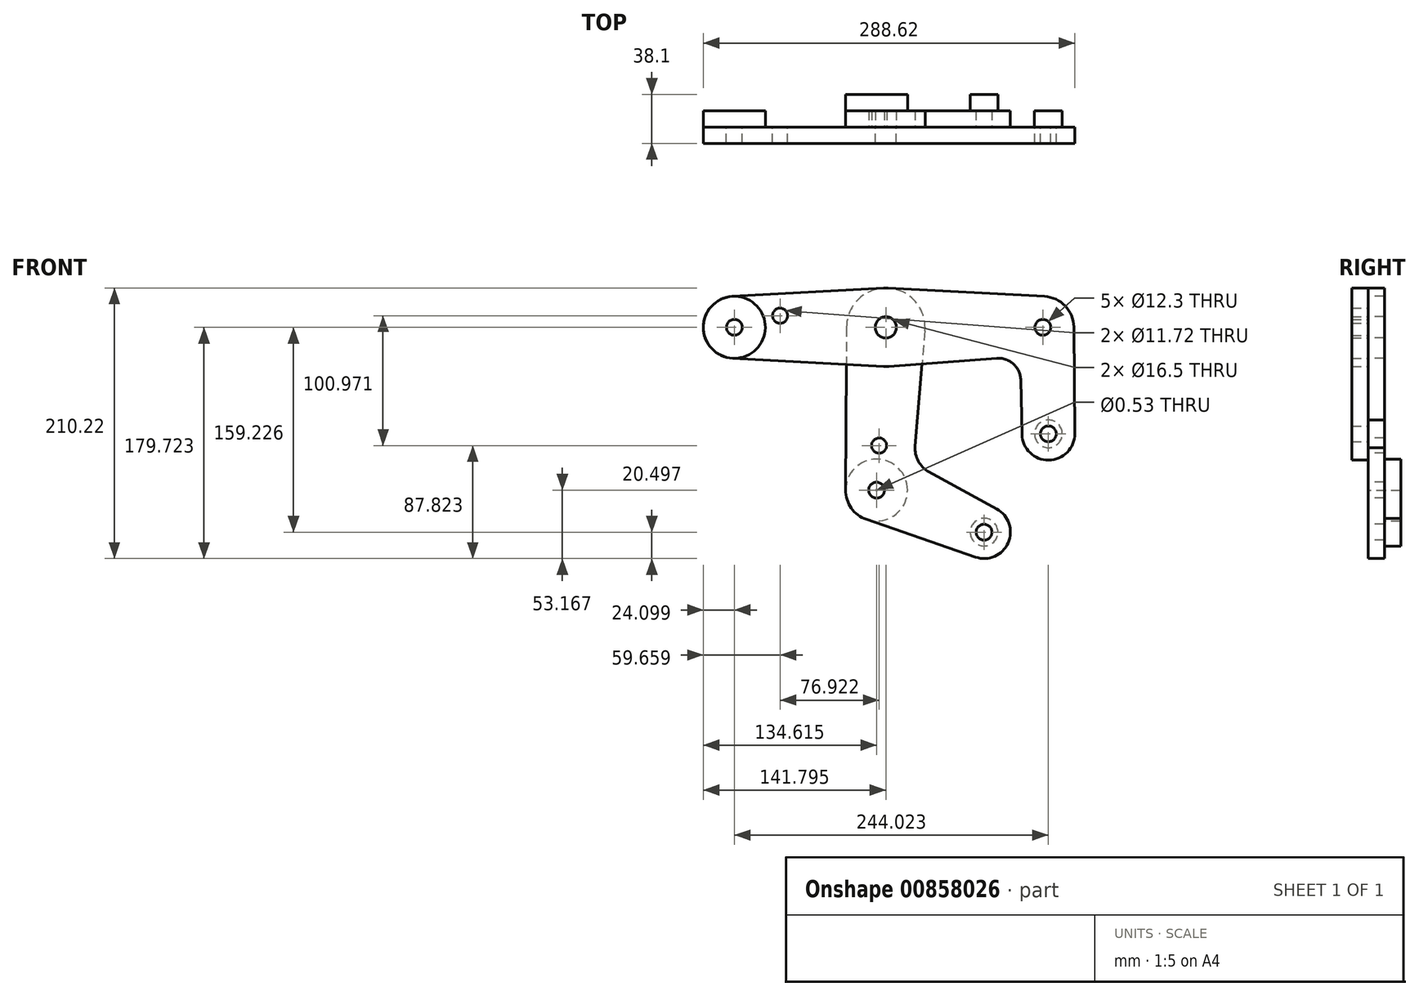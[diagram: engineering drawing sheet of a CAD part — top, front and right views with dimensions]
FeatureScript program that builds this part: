
annotation { "Feature Type Name" : "Feature", "Feature Type Description" : "" }
export const myFeature = defineFeature(function(context is Context, id is Id, definition is map)
    precondition{}
    {
        {
            var Q0;
            Q0=qCreatedBy(makeId("Front.planeOp"),FACE);
            var sketch = newSketch(context, id + "F0", { "sketchPlane" : qUnion([Q0])});
            skCircle(sketch, "E0", {"center": v(-43.4, 53.77) * mm, "radius": 30.5 * mm});
            skCircle(sketch, "E1", {"center": v(-161.1, 53.77) * mm, "radius": 24.1 * mm});
            skCircle(sketch, "E2", {"center": v(78.57, 53.77) * mm, "radius": 24.1 * mm});
            skCircle(sketch, "E3", {"center": v(-50.59, -72.78) * mm, "radius": 24.1 * mm});
            skCircle(sketch, "E4", {"center": v(32.9, -105.45) * mm, "radius": 20.5 * mm});
            skCircle(sketch, "E5", {"center": v(82.92, -29) * mm, "radius": 20.5 * mm});
            skCircle(sketch, "E6", {"center": v(-125.54, 62.84) * mm, "radius": 5.86 * mm});
            skCircle(sketch, "E7", {"center": v(-48.62, -38.13) * mm, "radius": 5.86 * mm});
            skLineSegment(sketch, "E8", {"start": v(-161.1, 53.77) * mm, "end": v(78.57, 53.77) * mm, "construction": true});
            skLineSegment(sketch, "E9", {"start": v(82.92, -29) * mm, "end": v(78.57, 53.77) * mm, "construction": true});
            skLineSegment(sketch, "E10", {"start": v(-50.59, -72.78) * mm, "end": v(32.9, -105.45) * mm, "construction": true});
            skLineSegment(sketch, "E11", {"start": v(-58.46, -95.56) * mm, "end": v(26.2, -124.83) * mm});
            skLineSegment(sketch, "E12", {"start": v(-162.41, 77.83) * mm, "end": v(-45.06, 84.22) * mm});
            skLineSegment(sketch, "E13", {"start": v(-41.8, 84.22) * mm, "end": v(79.84, 77.84) * mm});
            skLineSegment(sketch, "E14", {"start": v(-162.41, 29.71) * mm, "end": v(-45.06, 23.32) * mm});
            skLineSegment(sketch, "E15", {"start": v(-43.4, 53.77) * mm, "end": v(-50.59, -72.78) * mm, "construction": true});
            skLineSegment(sketch, "E16", {"start": v(-73.9, 53.96) * mm, "end": v(-74.68, -72.63) * mm});
            skLineSegment(sketch, "E17", {"start": v(102.67, 54) * mm, "end": v(103.42, -28.82) * mm});
            skCircle(sketch, "E18", {"center": v(-161.1, 53.77) * mm, "radius": 6.15 * mm});
            skCircle(sketch, "E19", {"center": v(-43.4, 53.77) * mm, "radius": 6.15 * mm});
            skCircle(sketch, "E20", {"center": v(78.57, 53.77) * mm, "radius": 6.15 * mm});
            skCircle(sketch, "E21", {"center": v(82.92, -29) * mm, "radius": 6.15 * mm});
            skCircle(sketch, "E22", {"center": v(32.9, -105.45) * mm, "radius": 6.15 * mm});
            skCircle(sketch, "E23", {"center": v(-50.59, -72.78) * mm, "radius": 6.15 * mm});
            skCircle(sketch, "E24", {"center": v(-43.4, 53.77) * mm, "radius": 8.25 * mm});
            skLineSegment(sketch, "E25", {"start": v(-41.08, 23.37) * mm, "end": v(42.63, 29.77) * mm});
            skLineSegment(sketch, "E26", {"start": v(62.43, -29.48) * mm, "end": v(61.45, 12.74) * mm});
            skArc(sketch, "E27", {"start": v(42.63, 29.77) * mm, "mid": v(55.7, 25.3) * mm, "end": v(61.45, 12.74) * mm});
            skLineSegment(sketch, "E28", {"start": v(-13.02, 51.2) * mm, "end": v(-20.63, -38.68) * mm});
            skLineSegment(sketch, "E29", {"start": v(42.76, -87.48) * mm, "end": v(-9.95, -58.58) * mm});
            skArc(sketch, "E30", {"start": v(-20.63, -38.68) * mm, "mid": v(-18.24, -50.22) * mm, "end": v(-9.95, -58.58) * mm});
            skSolve(sketch);
        }
        {
            var Q0;
            Q0=makeQuery(id+"F0.imprint","IMPRINT",FACE,{"disambiguationData":[TD([[makeQuery(id+"F0.imprint","IMPRINT",EDGE,{"derivedFrom":sQuery(id+"F0.wireOp",EDGE,"E18")}),-1.0]])]});
            var Q1;
            Q1=makeQuery(id+"F0.imprint","IMPRINT",FACE,{"disambiguationData":[TD([[makeQuery(id+"F0.imprint","IMPRINT",EDGE,{"derivedFrom":sQuery(id+"F0.wireOp",EDGE,"E6")}),-1.0]])]});
            var Q2;
            {var subQ0=sQuery(id+"F0.wireOp",EDGE,"E14");var subQ1=sQuery(id+"F0.wireOp",EDGE,"E0");var subQ2=makeQuery(id+"F0.imprint","INTERSECT",VERTEX,{"derivedFrom":[subQ1,subQ0]});Q2=makeQuery(id+"F0.imprint","IMPRINT",FACE,{"disambiguationData":[TD([[makeQuery(id+"F0.imprint","IMPRINT",EDGE,{"disambiguationData":[TD([[subQ2,1.0]])],"derivedFrom":subQ1}),-1.0]])]});}
            var Q3;
            Q3=makeQuery(id+"F0.imprint","IMPRINT",FACE,{"disambiguationData":[TD([[makeQuery(id+"F0.imprint","IMPRINT",EDGE,{"derivedFrom":sQuery(id+"F0.wireOp",EDGE,"E24")}),-1.0]])]});
            var Q4;
            {var subQ0=sQuery(id+"F0.wireOp",EDGE,"E25");var subQ1=sQuery(id+"F0.wireOp",EDGE,"E0");var subQ2=makeQuery(id+"F0.imprint","INTERSECT",VERTEX,{"derivedFrom":[subQ1,subQ0]});Q4=makeQuery(id+"F0.imprint","IMPRINT",FACE,{"disambiguationData":[TD([[makeQuery(id+"F0.imprint","IMPRINT",EDGE,{"disambiguationData":[TD([[subQ2,-1.0]])],"derivedFrom":subQ1}),-1.0]])]});}
            var Q5;
            {var subQ4=sQuery(id+"F0.wireOp",EDGE,"E13");Q5=makeQuery(id+"F0.imprint","IMPRINT",FACE,{"disambiguationData":[TD([[makeQuery(id+"F0.imprint","IMPRINT",EDGE,{"derivedFrom":subQ4}),-1.0]])]});}
            var Q6;
            Q6=makeQuery(id+"F0.imprint","IMPRINT",FACE,{"disambiguationData":[TD([[makeQuery(id+"F0.imprint","IMPRINT",EDGE,{"derivedFrom":sQuery(id+"F0.wireOp",EDGE,"E20")}),-1.0]])]});
            var Q7;
            Q7=makeQuery(id+"F0.imprint","IMPRINT",FACE,{"disambiguationData":[TD([[makeQuery(id+"F0.imprint","IMPRINT",EDGE,{"derivedFrom":sQuery(id+"F0.wireOp",EDGE,"E21")}),-1.0]])]});
            extrude(context, id + "F1", {"entities" : qUnion([Q0, Q1, Q2, Q3, Q4, Q5, Q6, Q7]), "depth" : 12.7 * mm, "offsetDistance" : 25 * mm});
        }
        {
            var Q0;
            Q0=makeQuery(id+"F0.imprint","IMPRINT",FACE,{"disambiguationData":[TD([[makeQuery(id+"F0.imprint","IMPRINT",EDGE,{"derivedFrom":sQuery(id+"F0.wireOp",EDGE,"E24")}),-1.0]])]});
            var Q1;
            {var subQ0=sQuery(id+"F0.wireOp",EDGE,"E25");var subQ1=sQuery(id+"F0.wireOp",EDGE,"E0");var subQ2=makeQuery(id+"F0.imprint","INTERSECT",VERTEX,{"derivedFrom":[subQ1,subQ0]});Q1=makeQuery(id+"F0.imprint","IMPRINT",FACE,{"disambiguationData":[TD([[makeQuery(id+"F0.imprint","IMPRINT",EDGE,{"disambiguationData":[TD([[subQ2,-1.0]])],"derivedFrom":subQ1}),-1.0]])]});}
            var Q2;
            {var subQ0=sQuery(id+"F0.wireOp",EDGE,"E14");var subQ1=sQuery(id+"F0.wireOp",EDGE,"E0");var subQ2=makeQuery(id+"F0.imprint","INTERSECT",VERTEX,{"derivedFrom":[subQ1,subQ0]});Q2=makeQuery(id+"F0.imprint","IMPRINT",FACE,{"disambiguationData":[TD([[makeQuery(id+"F0.imprint","IMPRINT",EDGE,{"disambiguationData":[TD([[subQ2,1.0]])],"derivedFrom":subQ1}),-1.0]])]});}
            var Q3;
            Q3=makeQuery(id+"F0.imprint","IMPRINT",FACE,{"disambiguationData":[TD([[makeQuery(id+"F0.imprint","IMPRINT",EDGE,{"derivedFrom":sQuery(id+"F0.wireOp",EDGE,"E7")}),-1.0]])]});
            var Q4;
            Q4=makeQuery(id+"F0.imprint","IMPRINT",FACE,{"disambiguationData":[TD([[makeQuery(id+"F0.imprint","IMPRINT",EDGE,{"derivedFrom":sQuery(id+"F0.wireOp",EDGE,"E23")}),-1.0]])]});
            var Q5;
            Q5=makeQuery(id+"F0.imprint","IMPRINT",FACE,{"disambiguationData":[TD([[makeQuery(id+"F0.imprint","IMPRINT",EDGE,{"derivedFrom":sQuery(id+"F0.wireOp",EDGE,"E22")}),-1.0]])]});
            extrude(context, id + "F2", {"entities" : qUnion([Q0, Q1, Q2, Q3, Q4, Q5]), "oppositeDirection" : true, "depth" : 12.7 * mm, "offsetDistance" : 25 * mm});
        }
        {
            var Q0;
            Q0=makeQuery(id+"F1.opExtrude","CAP_FACE",FACE,{"disambiguationData":[OSD([sQuery(id+"F0.wireOp",EDGE,"E0"),sQuery(id+"F0.wireOp",EDGE,"E1"),sQuery(id+"F0.wireOp",EDGE,"E2"),sQuery(id+"F0.wireOp",EDGE,"E5"),sQuery(id+"F0.wireOp",EDGE,"E6"),sQuery(id+"F0.wireOp",EDGE,"E12"),sQuery(id+"F0.wireOp",EDGE,"E13"),sQuery(id+"F0.wireOp",EDGE,"E14"),sQuery(id+"F0.wireOp",EDGE,"E17"),sQuery(id+"F0.wireOp",EDGE,"E18"),sQuery(id+"F0.wireOp",EDGE,"E20"),sQuery(id+"F0.wireOp",EDGE,"E21"),sQuery(id+"F0.wireOp",EDGE,"E24"),sQuery(id+"F0.wireOp",EDGE,"E25"),sQuery(id+"F0.wireOp",EDGE,"E26"),sQuery(id+"F0.wireOp",EDGE,"E27")])],"isStart":false});
            var sketch = newSketch(context, id + "F3", { "sketchPlane" : qUnion([Q0])});
            skCircle(sketch, "E31", {"center": v(82.92, -29) * mm, "radius": 10.76 * mm});
            skCircle(sketch, "E32", {"center": v(-161.1, 53.77) * mm, "radius": 24.1 * mm});
            skSolve(sketch);
        }
        {
            var Q0;
            Q0=makeQuery(id+"F0.imprint","IMPRINT",FACE,{"disambiguationData":[TD([[makeQuery(id+"F0.imprint","IMPRINT",EDGE,{"derivedFrom":sQuery(id+"F0.wireOp",EDGE,"E7")}),-1.0]])]});
            var sketch = newSketch(context, id + "F4", { "sketchPlane" : qUnion([Q0])});
            skCircle(sketch, "E33", {"center": v(-50.59, -72.78) * mm, "radius": 24.06 * mm});
            skCircle(sketch, "E34", {"center": v(-50.59, -72.78) * mm, "radius": 0.27 * mm});
            skCircle(sketch, "E35", {"center": v(32.9, -105.45) * mm, "radius": 10.76 * mm});
            skSolve(sketch);
        }
        {
            var Q0;
            Q0 = qSketchRegion(id + "F3", true);
            var Q1;
            Q1 = qSketchRegion(id + "F4", true);
            extrude(context, id + "F5", {"entities" : qUnion([Q0, Q1]), "oppositeDirection" : true, "depth" : 25.4 * mm, "offsetDistance" : 25 * mm});
        }
        {
            var Q0;
            Q0=makeQuery(id+"F1.opExtrude","SWEPT_BODY",BODY,{"disambiguationData":[OSD([sQuery(id+"F0.wireOp",EDGE,"E0"),sQuery(id+"F0.wireOp",EDGE,"E1"),sQuery(id+"F0.wireOp",EDGE,"E2"),sQuery(id+"F0.wireOp",EDGE,"E5"),sQuery(id+"F0.wireOp",EDGE,"E6"),sQuery(id+"F0.wireOp",EDGE,"E12"),sQuery(id+"F0.wireOp",EDGE,"E13"),sQuery(id+"F0.wireOp",EDGE,"E14"),sQuery(id+"F0.wireOp",EDGE,"E17"),sQuery(id+"F0.wireOp",EDGE,"E18"),sQuery(id+"F0.wireOp",EDGE,"E20"),sQuery(id+"F0.wireOp",EDGE,"E21"),sQuery(id+"F0.wireOp",EDGE,"E24"),sQuery(id+"F0.wireOp",EDGE,"E25"),sQuery(id+"F0.wireOp",EDGE,"E26"),sQuery(id+"F0.wireOp",EDGE,"E27")])]});
            var Q1;
            Q1=makeQuery(id+"F2.opExtrude","SWEPT_BODY",BODY,{"disambiguationData":[OSD([sQuery(id+"F0.wireOp",EDGE,"E0"),sQuery(id+"F0.wireOp",EDGE,"E3"),sQuery(id+"F0.wireOp",EDGE,"E4"),sQuery(id+"F0.wireOp",EDGE,"E7"),sQuery(id+"F0.wireOp",EDGE,"E11"),sQuery(id+"F0.wireOp",EDGE,"E16"),sQuery(id+"F0.wireOp",EDGE,"E22"),sQuery(id+"F0.wireOp",EDGE,"E23"),sQuery(id+"F0.wireOp",EDGE,"E24"),sQuery(id+"F0.wireOp",EDGE,"E28"),sQuery(id+"F0.wireOp",EDGE,"E29"),sQuery(id+"F0.wireOp",EDGE,"E30")])]});
            var Q2;
            Q2=makeQuery(id+"F5.opExtrude","SWEPT_BODY",BODY,{"disambiguationData":[OSD([sQuery(id+"F3.wireOp",EDGE,"E31")])]});
            var Q3;
            Q3=makeQuery(id+"F5.opExtrude","SWEPT_BODY",BODY,{"disambiguationData":[OSD([sQuery(id+"F4.wireOp",EDGE,"E35")])]});
            var Q4;
            Q4=makeQuery(id+"F5.opExtrude","SWEPT_BODY",BODY,{"disambiguationData":[OSD([sQuery(id+"F4.wireOp",EDGE,"E33"),sQuery(id+"F4.wireOp",EDGE,"E34")])]});
            var Q5;
            Q5=makeQuery(id+"F5.opExtrude","SWEPT_BODY",BODY,{"disambiguationData":[OSD([sQuery(id+"F3.wireOp",EDGE,"E32")])]});
            booleanBodies(context, id + "F6", {"operationType" : BooleanOperationType.SUBTRACTION, "tools" : qUnion([Q0, Q1]), "targets" : qUnion([Q2, Q3, Q4, Q5]), "keepTools" : true});
        }
    });
